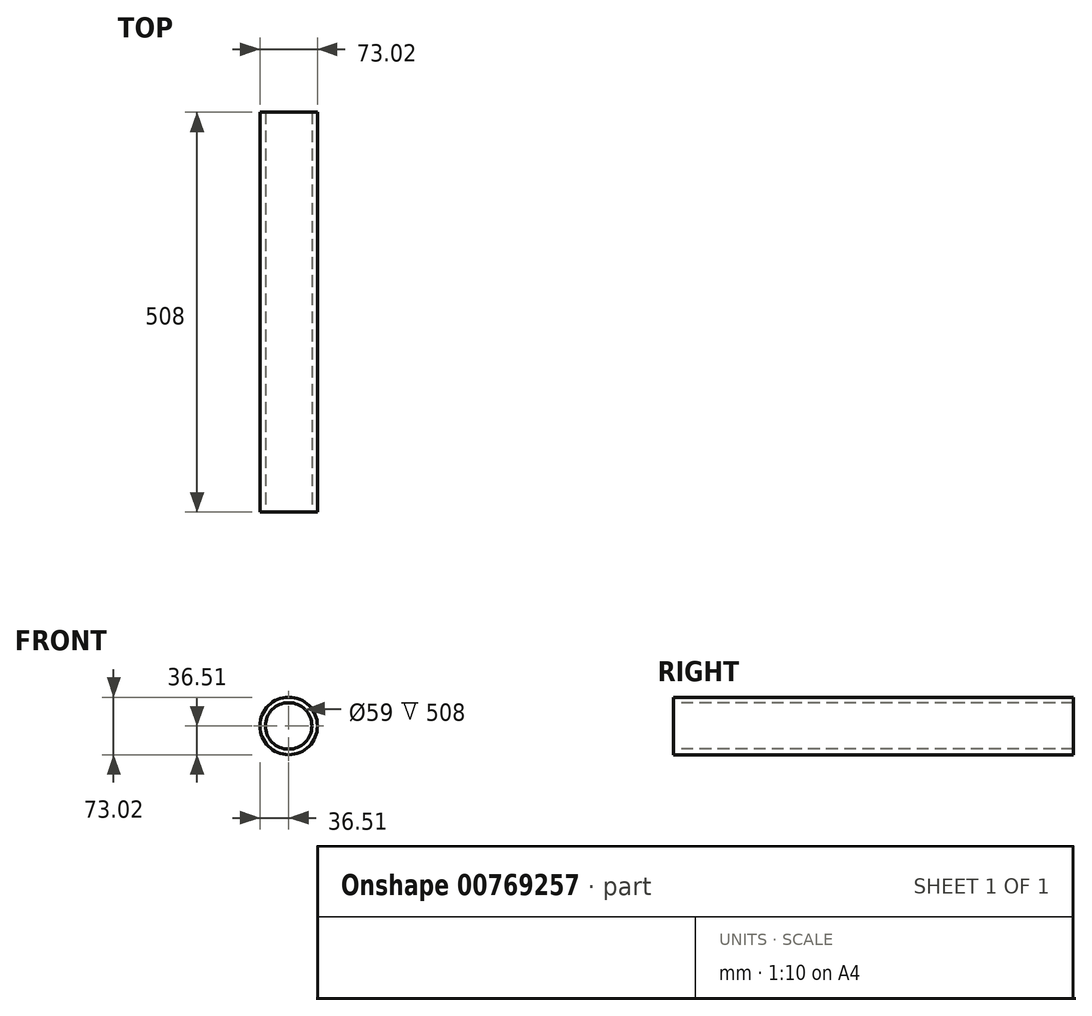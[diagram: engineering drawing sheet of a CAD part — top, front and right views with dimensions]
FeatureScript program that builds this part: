
annotation { "Feature Type Name" : "Feature", "Feature Type Description" : "" }
export const myFeature = defineFeature(function(context is Context, id is Id, definition is map)
    precondition{}
    {
        {
            var Q0;
            Q0=qCreatedBy(makeId("Front.planeOp"),FACE);
            var sketch = newSketch(context, id + "F0", { "sketchPlane" : qUnion([Q0])});
            skCircle(sketch, "E0", {"center": v(0, 0) * mm, "radius": 36.51 * mm});
            skCircle(sketch, "E1", {"center": v(0, 0) * mm, "radius": 29.5 * mm});
            skSolve(sketch);
        }
        {
            var Q0;
            Q0=makeQuery(id+"F0.imprint","IMPRINT",FACE,{"disambiguationData":[TD([[makeQuery(id+"F0.imprint","IMPRINT",EDGE,{"derivedFrom":sQuery(id+"F0.wireOp",EDGE,"E0")}),1.0]])]});
            extrude(context, id + "F1", {"entities" : qUnion([Q0]), "oppositeDirection" : true, "depth" : 508 * mm, "offsetDistance" : 25.4 * mm});
        }
    });
